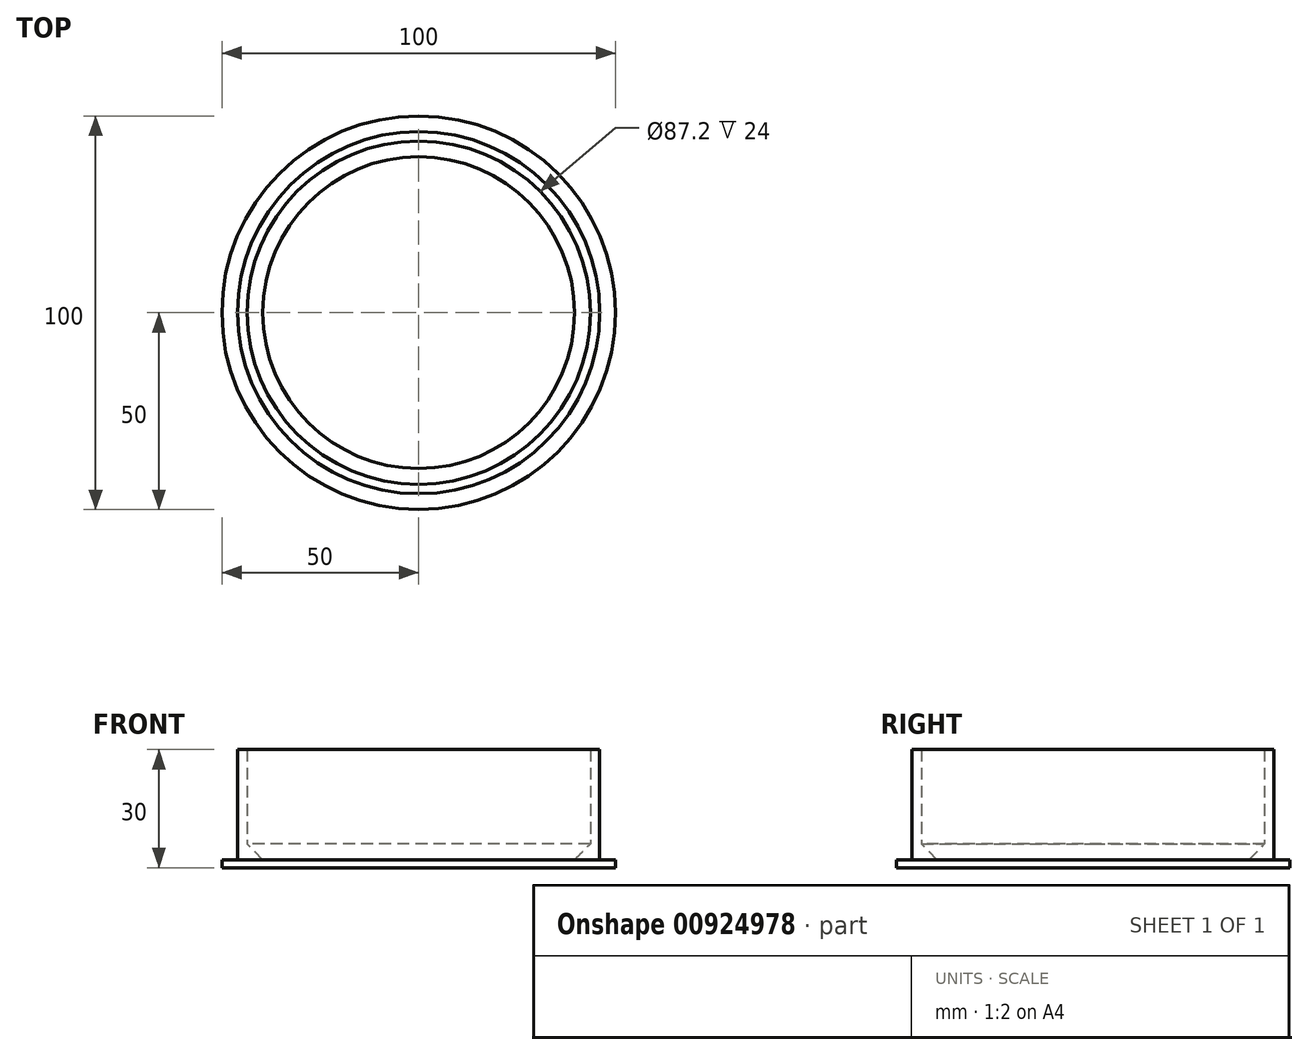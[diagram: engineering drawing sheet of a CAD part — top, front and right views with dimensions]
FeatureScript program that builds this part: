
annotation { "Feature Type Name" : "Feature", "Feature Type Description" : "" }
export const myFeature = defineFeature(function(context is Context, id is Id, definition is map)
    precondition{}
    {
        {
            var Q0;
            Q0=qCreatedBy(makeId("Top.planeOp"),FACE);
            var sketch = newSketch(context, id + "F0", { "sketchPlane" : qUnion([Q0])});
            skCircle(sketch, "E0", {"center": v(0, 0) * mm, "radius": 43.6 * mm});
            skCircle(sketch, "E1", {"center": v(0, 0) * mm, "radius": 46 * mm});
            skCircle(sketch, "E2", {"center": v(0, 0) * mm, "radius": 50 * mm});
            skCircle(sketch, "E3", {"center": v(0, 0) * mm, "radius": 2.2 * mm, "construction": true});
            skCircle(sketch, "E4", {"center": v(0, 0) * mm, "radius": 5 * mm, "construction": true});
            skSolve(sketch);
        }
        {
            var Q0;
            Q0=makeQuery(id+"F0.imprint","IMPRINT",FACE,{"disambiguationData":[TD([[makeQuery(id+"F0.imprint","IMPRINT",EDGE,{"derivedFrom":sQuery(id+"F0.wireOp",EDGE,"E0")}),1.0]])]});
            var Q1;
            Q1=makeQuery(id+"F0.imprint","IMPRINT",FACE,{"disambiguationData":[TD([[makeQuery(id+"F0.imprint","IMPRINT",EDGE,{"derivedFrom":sQuery(id+"F0.wireOp",EDGE,"E1")}),-1.0]])]});
            var Q2;
            Q2=makeQuery(id+"F0.imprint","IMPRINT",FACE,{"disambiguationData":[TD([[makeQuery(id+"F0.imprint","IMPRINT",EDGE,{"derivedFrom":sQuery(id+"F0.wireOp",EDGE,"E0")}),-1.0]])]});
            extrude(context, id + "F1", {"entities" : qUnion([Q0, Q1, Q2]), "depth" : 2 * mm, "offsetDistance" : 25 * mm});
        }
        {
            var Q0;
            Q0=makeQuery(id+"F0.imprint","IMPRINT",FACE,{"disambiguationData":[TD([[makeQuery(id+"F0.imprint","IMPRINT",EDGE,{"derivedFrom":sQuery(id+"F0.wireOp",EDGE,"E0")}),-1.0]])]});
            extrude(context, id + "F2", {"entities" : qUnion([Q0]), "operationType" : NewBodyOperationType.ADD, "depth" : 30 * mm, "offsetDistance" : 25 * mm});
        }
        {
            var Q0;
            Q0=makeQuery(id+"F1.opExtrude","CAP_EDGE",EDGE,{"disambiguationData":[OSD([sQuery(id+"F0.wireOp",EDGE,"E4")])],"isStart":false});
            var Q1;
            Q1=makeQuery(id+"F2.boolean.opBoolean","INTERSECT",EDGE,{"derivedFrom":[makeQuery(id+"F1.opExtrude","CAP_FACE",FACE,{"disambiguationData":[OSD([sQuery(id+"F0.wireOp",EDGE,"E2"),sQuery(id+"F0.wireOp",EDGE,"E4")])],"isStart":false}),makeQuery(id+"F2.opExtrude","SWEPT_FACE",FACE,{"disambiguationData":[OSD([sQuery(id+"F0.wireOp",EDGE,"E0")])]})]});
            chamfer(context, id + "F3", {"entities" : qUnion([Q0, Q1]), "width" : 4 * mm, "tangentPropagation" : true});
        }
    });
